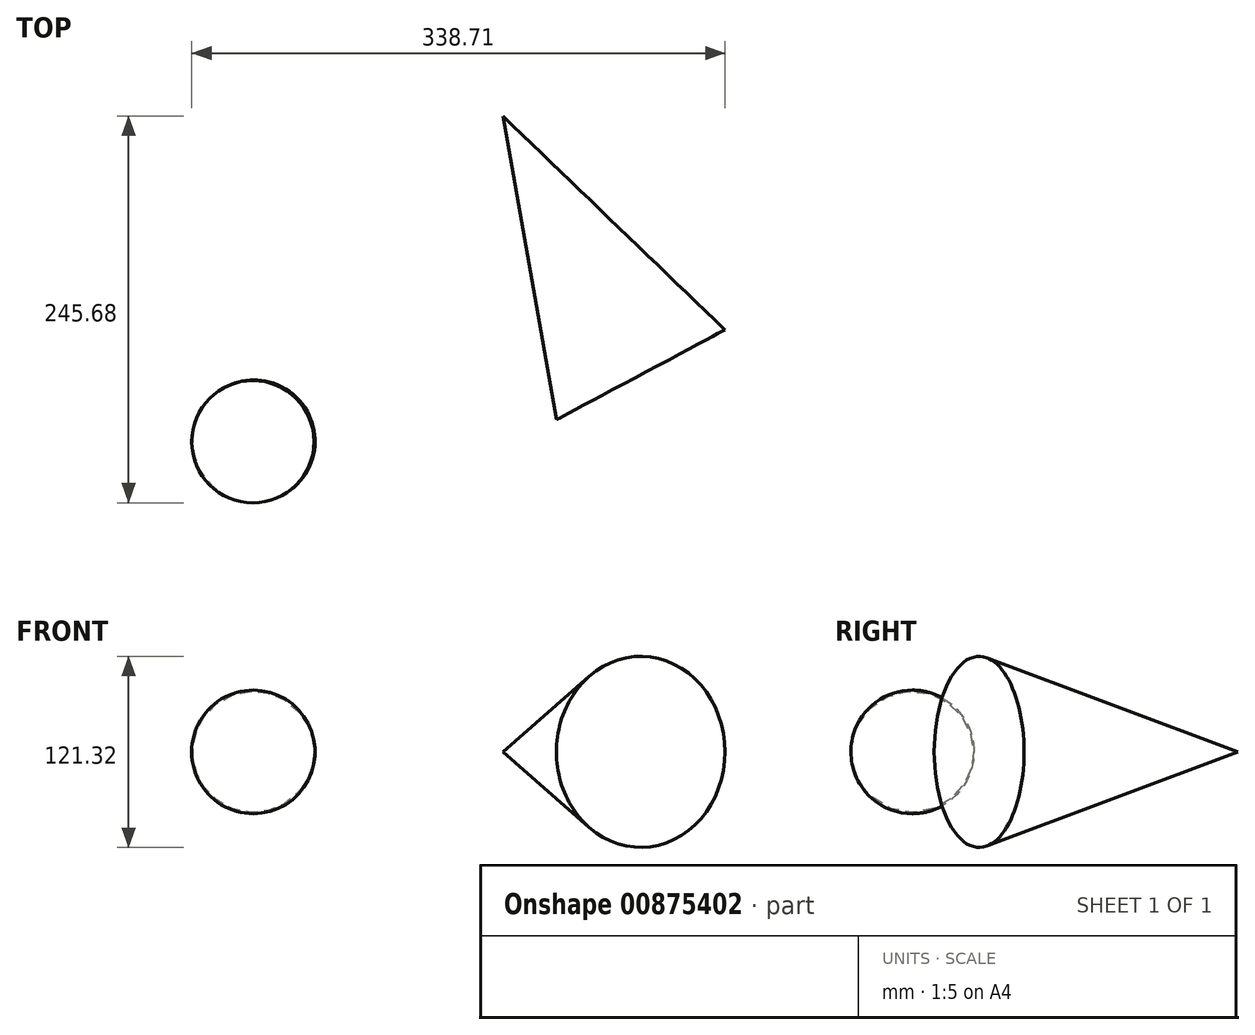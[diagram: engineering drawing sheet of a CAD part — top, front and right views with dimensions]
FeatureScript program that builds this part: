
annotation { "Feature Type Name" : "Feature", "Feature Type Description" : "" }
export const myFeature = defineFeature(function(context is Context, id is Id, definition is map)
    precondition{}
    {
        {
            var Q0;
            Q0=qCreatedBy(makeId("Top.planeOp"),FACE);
            var sketch = newSketch(context, id + "F0", { "sketchPlane" : qUnion([Q0])});
            skLineSegment(sketch, "E0", {"start": v(-87.54, 164.28) * mm, "end": v(0, 0) * mm});
            skLineSegment(sketch, "E1", {"start": v(0, 0) * mm, "end": v(53.53, 28.53) * mm});
            skLineSegment(sketch, "E2", {"start": v(53.53, 28.53) * mm, "end": v(-87.54, 164.28) * mm});
            skSolve(sketch);
        }
        {
            var Q0;
            Q0 = qSketchRegion(id + "F0", true);
            var Q1;
            Q1=sQuery(id+"F0.wireOp",EDGE,"E0");
            revolve(context, id + "F1", {"surfaceOperationType" : NewSurfaceOperationType.NEW, "entities" : qUnion([Q0]), "axis" : qUnion([Q1]), "revolveType" : RevolveType.FULL});
        }
        {
            var Q0;
            Q0=qCreatedBy(makeId("Top.planeOp"),FACE);
            var sketch = newSketch(context, id + "F2", { "sketchPlane" : qUnion([Q0])});
            skCircle(sketch, "E3", {"center": v(-245.68, -42.18) * mm, "radius": 38.86 * mm});
            skLineSegment(sketch, "E4", {"start": v(-264.8, -8.34) * mm, "end": v(-227.2, -76.37) * mm});
            skSolve(sketch);
        }
        {
            var Q0;
            {var subQ0=sQuery(id+"F2.wireOp",EDGE,"E4");Q0=makeQuery(id+"F2.imprint","IMPRINT",FACE,{"disambiguationData":[TD([[makeQuery(id+"F2.imprint","IMPRINT",EDGE,{"derivedFrom":subQ0}),1.0]])]});}
            var Q1;
            Q1=sQuery(id+"F2.wireOp",EDGE,"E4");
            revolve(context, id + "F3", {"surfaceOperationType" : NewSurfaceOperationType.NEW, "entities" : qUnion([Q0]), "axis" : qUnion([Q1]), "revolveType" : RevolveType.FULL});
        }
    });
